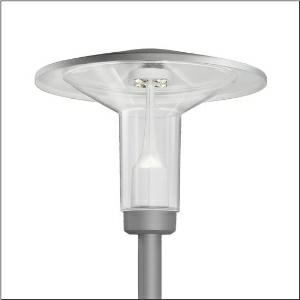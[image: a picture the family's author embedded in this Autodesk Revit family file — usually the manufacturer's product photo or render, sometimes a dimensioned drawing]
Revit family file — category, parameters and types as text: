
# Revit family: laterne_iq___st1_2a_5xa5255mf14hp_8067
name_source: partatom
category: Lighting Fixtures
units: mm (PartAtom-declared; Revit-internal decimal feet)

## family parameters
Cut with Voids When Loaded = No
Host = Face
Light Source = No
Part Type = Normal
Room Calculation Point = No
Round Connector Dimension = Use Diameter
Shared = No

## types (1)
- --- (1 x LED, 4240 lm, 33.6 W, 2700K)
    Apparent Load = 34 VA
    CIE Flux Codes = 25 63 94 98 100
    Color Rendering = 70
    Color Temperature = 2700K
    Default Elevation = 1800 mm
    Description = Lantern iQ, mast luminaire, Module 540 iQ-SR, primary light control with 3 zone facetted reflector, of plastic, silver coated, highly specular, structured, primary optical cover: cover, of PMMA, transparent, light distribution: ST1.2a, light emission: direct distribution, primary light characteristic: asymmetric, installation type: post-top, LED, High Power LED, rated luminous flux: 4.240lm, luminous efficacy: 126lm/W, light colour: 727, colour temperature: 2700K, control gear: iQ Street-Remote, control: pre-setting: logarithmic dimming characteristic, Street-Remote, Auto-Match, Temp-Guard, Lumen-Switch, Night-Set, Smart-Wire, Light-Fading, Desk-Remote (wireless, voltage-free reading and setting of iQ features in the workshop via application-optimized NFC function/RFID function), optimised constant luminous flux control (CLO 2.0), with terminal, 6-pole, max. 2.5mm², mains connection: 230..240V, AC, 50/60Hz, start of lifetime: 34W, end of service life: 36W, reduction: 15W, luminaire housing, upper part, of glass-fibre reinforced polyester, coated, Siteco® metallic grey (DB 702S), diameter: 750mm, height: 583mm, spigot size: d x l = 76 x 70mm (post-top) | with reducer (optional accessory) 60 x 70mm, mounting height: 3..5m, post-top mast mounting element, of diecast aluminium, coated, Siteco® metallic grey (DB 702S), Module 540 iQ-SR, traffic white (RAL 9016), equipment: Power, protection rating (complete): IP65, insulation class (complete): insulation class II (safety insulation), certification: CE, ENEC, VDE, packaging unit: 1 piece

Light Distribution: ST1.2a
    Height = 583 mm
    Lamp = 1 x LED
    Lamp Light Flux = 4240 lm
    Lamp Power = 33.6 W
    Lamp count = 1
    Length = 750 mm
    Luminous efficacy = 126 lm/W
    Manufacturer = Siteco
    ModVariant = No
    Model = 5XA5255MF14HP
    Number of Poles = 1
    OnlyDefault = Yes
    Power Factor = 1
    Product Name = Laterne iQ | ST1.2a
    Product group = mast luminaire | pylon top
    ProductGroupID = 6100
    Protection Class = Protection class II
    Protection Degree = IP 65
    RLX_Detail_Level = 1
    RLX_Emergency_Light_Flux = 0 lm
    RLX_Emergency_Type = 0
    RLX_Emergency_Type_DB = No
    RlxData = <blob elided: 34257 chars, md5=be4dc093>
    Socket = socket
    Standby Power = 0 W
    System Light Flux = 4240 lm
    System Power = 34 W
    Type Comments = factory setting: luminous flux: 100 % | dim-lin: 254 | 695 mA
    Type Image = l_1006050.jpg
    URL = http://relux.com
    VarID = @adj_152770
    Voltage = 0 V
    Weight = 0.00 kg
    Width = 0 mm  [stored 0 ft]

note: [stored X ft] marks values corroborated as IEEE doubles in the binary element streams (Revit-internal decimal feet)

## geometry (parser evidence)
native form markers: Blend x4, Sweep x11
no freeform markers — native parametric forms only
